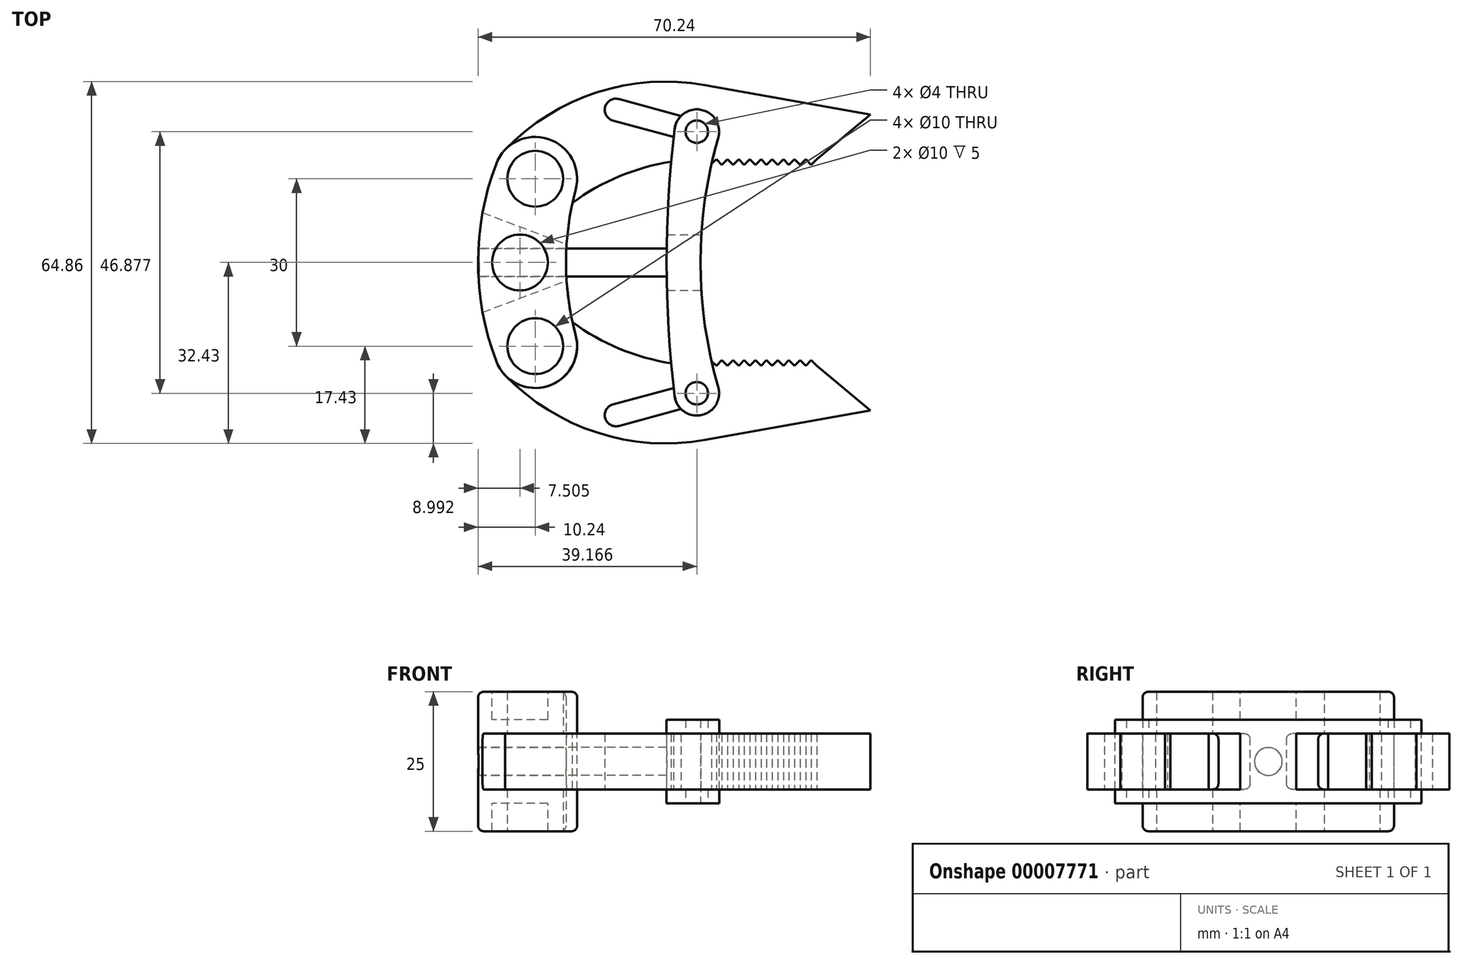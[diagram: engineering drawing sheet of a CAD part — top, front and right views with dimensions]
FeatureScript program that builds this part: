
annotation { "Feature Type Name" : "Feature", "Feature Type Description" : "" }
export const myFeature = defineFeature(function(context is Context, id is Id, definition is map)
    precondition{}
    {
        {
            var Q0;
            Q0=qCreatedBy(makeId("Top.planeOp"),FACE);
            var sketch = newSketch(context, id + "F0", { "sketchPlane" : qUnion([Q0])});
            skLineSegment(sketch, "E0", {"start": v(0, -15) * mm, "end": v(0, 15) * mm, "construction": true});
            skArc(sketch, "E1", {"start": v(7.24, 13.04) * mm, "mid": v(2.3, 22.14) * mm, "end": v(-7.02, 17.65) * mm});
            skArc(sketch, "E2", {"start": v(-7.02, -17.65) * mm, "mid": v(2.3, -22.14) * mm, "end": v(7.24, -13.04) * mm});
            skArc(sketch, "E3", {"start": v(-7.02, 17.65) * mm, "mid": v(-10.24, 0) * mm, "end": v(-7.02, -17.65) * mm});
            skArc(sketch, "E4", {"start": v(7.24, 13.04) * mm, "mid": v(5.5, 0) * mm, "end": v(7.24, -13.04) * mm});
            skCircle(sketch, "E5", {"center": v(0, 15) * mm, "radius": 5 * mm});
            skCircle(sketch, "E6", {"center": v(0, -15) * mm, "radius": 5 * mm});
            skSolve(sketch);
        }
        {
            var Q0;
            Q0=qCreatedBy(makeId("Top.planeOp"),FACE);
            var sketch = newSketch(context, id + "F1", { "sketchPlane" : qUnion([Q0])});
            skArc(sketch, "E7", {"start": v(-5.4, 20.2) * mm, "mid": v(-5.5, 9.9) * mm, "end": v(4.8, 9.24) * mm});
            skArc(sketch, "E8", {"start": v(30.42, 31.8) * mm, "mid": v(11.06, 30.48) * mm, "end": v(-5.4, 20.2) * mm});
            skLineSegment(sketch, "E9", {"start": v(30.42, 31.8) * mm, "end": v(60, 26.52) * mm});
            skArc(sketch, "E10", {"start": v(30.42, 18.52) * mm, "mid": v(16.8, 16.13) * mm, "end": v(4.8, 9.24) * mm});
            skLineSegment(sketch, "E11", {"start": v(30.42, 18.52) * mm, "end": v(50.42, 18.52) * mm, "construction": true});
            skLineSegment(sketch, "E12", {"start": v(60, 26.52) * mm, "end": v(50.42, 18.52) * mm});
            skCircle(sketch, "E13.0", {"center": v(0, 15) * mm, "radius": 5 * mm});
            skLineSegment(sketch, "E14", {"start": v(0, 0) * mm, "end": v(62.82, 0) * mm, "construction": true});
            skArc(sketch, "E15.0.MirrorCS", {"start": v(-5.4, -20.2) * mm, "mid": v(-5.5, -9.9) * mm, "end": v(4.8, -9.24) * mm});
            skArc(sketch, "E15.1.MirrorCS", {"start": v(30.42, -18.52) * mm, "mid": v(16.8, -16.13) * mm, "end": v(4.8, -9.24) * mm});
            skArc(sketch, "E15.2.MirrorCS", {"start": v(30.42, -31.8) * mm, "mid": v(11.06, -30.48) * mm, "end": v(-5.4, -20.2) * mm});
            skCircle(sketch, "E15.3.MirrorC", {"center": v(0, -15) * mm, "radius": 5 * mm});
            skLineSegment(sketch, "E15.4.MirrorCS", {"start": v(60, -26.52) * mm, "end": v(50.42, -18.52) * mm});
            skLineSegment(sketch, "E15.5.MirrorCS", {"start": v(30.42, -18.52) * mm, "end": v(50.42, -18.52) * mm, "construction": true});
            skLineSegment(sketch, "E15.6.MirrorCS", {"start": v(30.42, -31.8) * mm, "end": v(60, -26.52) * mm});
            skLineSegment(sketch, "E16", {"start": v(30.42, -18.52) * mm, "end": v(31.42, -17.52) * mm});
            skLineSegment(sketch, "E17", {"start": v(31.42, -17.52) * mm, "end": v(32.42, -18.52) * mm});
            skLineSegment(sketch, "E18.1.0.0", {"start": v(32.42, -18.52) * mm, "end": v(33.42, -17.52) * mm});
            skLineSegment(sketch, "E18.1.0.1", {"start": v(33.42, -17.52) * mm, "end": v(34.42, -18.52) * mm});
            skLineSegment(sketch, "E18.2.0.0", {"start": v(34.42, -18.52) * mm, "end": v(35.42, -17.52) * mm});
            skLineSegment(sketch, "E18.2.0.1", {"start": v(35.42, -17.52) * mm, "end": v(36.42, -18.52) * mm});
            skLineSegment(sketch, "E18.3.0.0", {"start": v(36.42, -18.52) * mm, "end": v(37.42, -17.52) * mm});
            skLineSegment(sketch, "E18.3.0.1", {"start": v(37.42, -17.52) * mm, "end": v(38.42, -18.52) * mm});
            skLineSegment(sketch, "E18.4.0.0", {"start": v(38.42, -18.52) * mm, "end": v(39.42, -17.52) * mm});
            skLineSegment(sketch, "E18.4.0.1", {"start": v(39.42, -17.52) * mm, "end": v(40.42, -18.52) * mm});
            skLineSegment(sketch, "E18.5.0.0", {"start": v(40.42, -18.52) * mm, "end": v(41.42, -17.52) * mm});
            skLineSegment(sketch, "E18.5.0.1", {"start": v(41.42, -17.52) * mm, "end": v(42.42, -18.52) * mm});
            skLineSegment(sketch, "E18.6.0.0", {"start": v(42.42, -18.52) * mm, "end": v(43.42, -17.52) * mm});
            skLineSegment(sketch, "E18.6.0.1", {"start": v(43.42, -17.52) * mm, "end": v(44.42, -18.52) * mm});
            skLineSegment(sketch, "E18.7.0.0", {"start": v(44.42, -18.52) * mm, "end": v(45.42, -17.52) * mm});
            skLineSegment(sketch, "E18.7.0.1", {"start": v(45.42, -17.52) * mm, "end": v(46.42, -18.52) * mm});
            skLineSegment(sketch, "E18.8.0.0", {"start": v(46.42, -18.52) * mm, "end": v(47.42, -17.52) * mm});
            skLineSegment(sketch, "E18.8.0.1", {"start": v(47.42, -17.52) * mm, "end": v(48.42, -18.52) * mm});
            skLineSegment(sketch, "E18.9.0.0", {"start": v(48.42, -18.52) * mm, "end": v(49.42, -17.52) * mm});
            skLineSegment(sketch, "E18.9.0.1", {"start": v(49.42, -17.52) * mm, "end": v(50.42, -18.52) * mm});
            skLineSegment(sketch, "E18.direction1", {"start": v(30.42, -18.52) * mm, "end": v(32.42, -18.52) * mm, "construction": true});
            skLineSegment(sketch, "E19", {"start": v(30.42, 18.52) * mm, "end": v(31.42, 17.52) * mm});
            skLineSegment(sketch, "E20", {"start": v(31.42, 17.52) * mm, "end": v(32.42, 18.52) * mm});
            skLineSegment(sketch, "E21.1.0.0", {"start": v(32.42, 18.52) * mm, "end": v(33.42, 17.52) * mm});
            skLineSegment(sketch, "E21.1.0.1", {"start": v(33.42, 17.52) * mm, "end": v(34.42, 18.52) * mm});
            skLineSegment(sketch, "E21.2.0.0", {"start": v(34.42, 18.52) * mm, "end": v(35.42, 17.52) * mm});
            skLineSegment(sketch, "E21.2.0.1", {"start": v(35.42, 17.52) * mm, "end": v(36.42, 18.52) * mm});
            skLineSegment(sketch, "E21.3.0.0", {"start": v(36.42, 18.52) * mm, "end": v(37.42, 17.52) * mm});
            skLineSegment(sketch, "E21.3.0.1", {"start": v(37.42, 17.52) * mm, "end": v(38.42, 18.52) * mm});
            skLineSegment(sketch, "E21.4.0.0", {"start": v(38.42, 18.52) * mm, "end": v(39.42, 17.52) * mm});
            skLineSegment(sketch, "E21.4.0.1", {"start": v(39.42, 17.52) * mm, "end": v(40.42, 18.52) * mm});
            skLineSegment(sketch, "E21.5.0.0", {"start": v(40.42, 18.52) * mm, "end": v(41.42, 17.52) * mm});
            skLineSegment(sketch, "E21.5.0.1", {"start": v(41.42, 17.52) * mm, "end": v(42.42, 18.52) * mm});
            skLineSegment(sketch, "E21.6.0.0", {"start": v(42.42, 18.52) * mm, "end": v(43.42, 17.52) * mm});
            skLineSegment(sketch, "E21.6.0.1", {"start": v(43.42, 17.52) * mm, "end": v(44.42, 18.52) * mm});
            skLineSegment(sketch, "E21.7.0.0", {"start": v(44.42, 18.52) * mm, "end": v(45.42, 17.52) * mm});
            skLineSegment(sketch, "E21.7.0.1", {"start": v(45.42, 17.52) * mm, "end": v(46.42, 18.52) * mm});
            skLineSegment(sketch, "E21.8.0.0", {"start": v(46.42, 18.52) * mm, "end": v(47.42, 17.52) * mm});
            skLineSegment(sketch, "E21.8.0.1", {"start": v(47.42, 17.52) * mm, "end": v(48.42, 18.52) * mm});
            skLineSegment(sketch, "E21.9.0.0", {"start": v(48.42, 18.52) * mm, "end": v(49.42, 17.52) * mm});
            skLineSegment(sketch, "E21.9.0.1", {"start": v(49.42, 17.52) * mm, "end": v(50.42, 18.52) * mm});
            skLineSegment(sketch, "E21.direction1", {"start": v(31.42, 17.52) * mm, "end": v(33.42, 17.52) * mm, "construction": true});
            skArc(sketch, "E22", {"start": v(14.97, 29.28) * mm, "mid": v(12.52, 27.88) * mm, "end": v(13.92, 25.42) * mm});
            skArc(sketch, "E23", {"start": v(28.4, 21.5) * mm, "mid": v(30.86, 22.92) * mm, "end": v(29.45, 25.37) * mm});
            skLineSegment(sketch, "E24", {"start": v(14.97, 29.28) * mm, "end": v(29.45, 25.37) * mm});
            skLineSegment(sketch, "E25", {"start": v(13.92, 25.42) * mm, "end": v(28.4, 21.5) * mm});
            skLineSegment(sketch, "E26", {"start": v(14.45, 27.35) * mm, "end": v(28.93, 23.44) * mm, "construction": true});
            skArc(sketch, "E27.1.MirrorCS", {"start": v(13.92, 25.42) * mm, "mid": v(12.52, 27.88) * mm, "end": v(14.97, 29.28) * mm});
            skArc(sketch, "E27.2.MirrorCS", {"start": v(29.45, 25.37) * mm, "mid": v(30.86, 22.92) * mm, "end": v(28.4, 21.5) * mm});
            skArc(sketch, "E28.0.MirrorCS", {"start": v(29.45, -25.37) * mm, "mid": v(30.86, -22.92) * mm, "end": v(28.4, -21.5) * mm});
            skLineSegment(sketch, "E28.1.MirrorCS", {"start": v(14.97, -29.28) * mm, "end": v(29.45, -25.37) * mm});
            skArc(sketch, "E28.2.MirrorCS", {"start": v(14.97, -29.28) * mm, "mid": v(12.52, -27.88) * mm, "end": v(13.92, -25.42) * mm});
            skLineSegment(sketch, "E28.3.MirrorCS", {"start": v(13.92, -25.42) * mm, "end": v(28.4, -21.5) * mm});
            skLineSegment(sketch, "E29", {"start": v(30.42, 31.8) * mm, "end": v(28.93, 23.44) * mm, "construction": true});
            skSolve(sketch);
        }
        {
            var Q0;
            Q0 = qSketchRegion(id + "F0", true);
            extrude(context, id + "F2", {"entities" : qUnion([Q0]), "endBound" : BoundingType.SYMMETRIC, "depth" : 25 * mm});
        }
        {
            var Q0;
            Q0 = qSketchRegion(id + "F1", true);
            extrude(context, id + "F3", {"entities" : qUnion([Q0]), "endBound" : BoundingType.SYMMETRIC, "depth" : 10 * mm});
        }
        {
            var Q0;
            Q0=makeQuery(id+"F2.opExtrude","CAP_FACE",FACE,{"disambiguationData":[OSD([sQuery(id+"F0.wireOp",EDGE,"E1"),sQuery(id+"F0.wireOp",EDGE,"E2"),sQuery(id+"F0.wireOp",EDGE,"E3"),sQuery(id+"F0.wireOp",EDGE,"E4"),sQuery(id+"F0.wireOp",EDGE,"E5"),sQuery(id+"F0.wireOp",EDGE,"E6")])],"isStart":false});
            var sketch = newSketch(context, id + "F4", { "sketchPlane" : qUnion([Q0])});
            skArc(sketch, "E30", {"start": v(0, 15) * mm, "mid": v(-2.74, 0) * mm, "end": v(0, -15) * mm, "construction": true});
            skCircle(sketch, "E31", {"center": v(-2.74, 0) * mm, "radius": 5 * mm});
            skSolve(sketch);
        }
        {
            var Q0;
            Q0 = qSketchRegion(id + "F4", true);
            extrude(context, id + "F5", {"entities" : qUnion([Q0]), "operationType" : NewBodyOperationType.REMOVE, "endBound" : BoundingType.THROUGH_ALL, "oppositeDirection" : true, "depth" : 25 * mm});
        }
        {
            var Q0;
            Q0=qCreatedBy(makeId("Top.planeOp"),FACE);
            var sketch = newSketch(context, id + "F6", { "sketchPlane" : qUnion([Q0])});
            skCircle(sketch, "E32.0", {"center": v(-2.74, 0) * mm, "radius": 6 * mm, "construction": true});
            skCircle(sketch, "E33", {"center": v(0, 15) * mm, "radius": 9 * mm, "construction": true});
            skLineSegment(sketch, "E34", {"start": v(-9.43, 8.94) * mm, "end": v(5.62, 3.26) * mm});
            skArc(sketch, "E35.0", {"start": v(-7.02, 17.65) * mm, "mid": v(-8.42, 13.35) * mm, "end": v(-9.43, 8.94) * mm});
            skArc(sketch, "E36.0", {"start": v(7.24, 13.04) * mm, "mid": v(6.18, 8.2) * mm, "end": v(5.62, 3.26) * mm});
            skPoint(sketch, "E37.orphan", {"position": v(-7.02, -17.65) * mm});
            skPoint(sketch, "E38.orphan", {"position": v(7.24, -13.04) * mm});
            skLineSegment(sketch, "E39", {"start": v(-2.74, 0) * mm, "end": v(16.54, 0) * mm, "construction": true});
            skLineSegment(sketch, "E40.0.MirrorCS", {"start": v(-9.43, -8.94) * mm, "end": v(5.62, -3.26) * mm});
            skArc(sketch, "E41.0", {"start": v(7.24, 13.04) * mm, "mid": v(2.3, 22.14) * mm, "end": v(-7.02, 17.65) * mm});
            skArc(sketch, "E42.0", {"start": v(-7.02, -17.65) * mm, "mid": v(2.3, -22.14) * mm, "end": v(7.24, -13.04) * mm});
            skArc(sketch, "E43.0.MirrorCS", {"start": v(7.24, -13.04) * mm, "mid": v(6.18, -8.2) * mm, "end": v(5.62, -3.26) * mm});
            skArc(sketch, "E43.1.MirrorCS", {"start": v(-7.02, -17.65) * mm, "mid": v(-8.42, -13.35) * mm, "end": v(-9.43, -8.94) * mm});
            skSolve(sketch);
        }
        {
            var Q0;
            Q0 = qSketchRegion(id + "F6", true);
            extrude(context, id + "F7", {"entities" : qUnion([Q0]), "operationType" : NewBodyOperationType.REMOVE, "endBound" : BoundingType.SYMMETRIC, "oppositeDirection" : true, "depth" : 10 * mm});
        }
        {
            var Q0;
            Q0=qCreatedBy(makeId("Top.planeOp"),FACE);
            var sketch = newSketch(context, id + "F8", { "sketchPlane" : qUnion([Q0])});
            skCircle(sketch, "E44.0", {"center": v(-2.74, 0) * mm, "radius": 5 * mm});
            skSolve(sketch);
        }
        {
            var Q0;
            Q0 = qSketchRegion(id + "F8", true);
            extrude(context, id + "F9", {"entities" : qUnion([Q0]), "operationType" : NewBodyOperationType.ADD, "endBound" : BoundingType.SYMMETRIC, "depth" : 15 * mm});
        }
        {
            var Q0;
            Q0=qCreatedBy(makeId("Right.planeOp"),FACE);
            var sketch = newSketch(context, id + "F10", { "sketchPlane" : qUnion([Q0])});
            skCircle(sketch, "E45", {"center": v(0, 0) * mm, "radius": 2.5 * mm});
            skSolve(sketch);
        }
        {
            var Q0;
            Q0 = qSketchRegion(id + "F10", true);
            extrude(context, id + "F11", {"entities" : qUnion([Q0]), "operationType" : NewBodyOperationType.REMOVE, "endBound" : BoundingType.THROUGH_ALL, "oppositeDirection" : true, "depth" : 25 * mm, "hasSecondDirection" : true, "secondDirectionBound" : SecondDirectionBoundingType.THROUGH_ALL, "secondDirectionOppositeDirection" : false, "secondDirectionDepth" : 25 * mm});
        }
        {
            var Q0;
            Q0=qCreatedBy(makeId("Right.planeOp"),FACE);
            var sketch = newSketch(context, id + "F12", { "sketchPlane" : qUnion([Q0])});
            skCircle(sketch, "E46.0", {"center": v(0, 0) * mm, "radius": 2.5 * mm});
            skSolve(sketch);
        }
        {
            var Q0;
            Q0 = qSketchRegion(id + "F12", true);
            extrude(context, id + "F13", {"entities" : qUnion([Q0]), "depth" : 27 * mm, "hasSecondDirection" : true, "secondDirectionOppositeDirection" : true, "secondDirectionDepth" : 10 * mm});
        }
        {
            var Q0;
            Q0=qCreatedBy(makeId("Top.planeOp"),FACE);
            var sketch = newSketch(context, id + "F14", { "sketchPlane" : qUnion([Q0])});
            skLineSegment(sketch, "E47", {"start": v(0, 0) * mm, "end": v(36.42, 0) * mm, "construction": true});
            skArc(sketch, "E48", {"start": v(32.77, 22.32) * mm, "mid": v(29.73, 27.36) * mm, "end": v(24.95, 23.92) * mm});
            skArc(sketch, "E49", {"start": v(24.95, 23.92) * mm, "mid": v(23.52, 0) * mm, "end": v(24.95, -23.92) * mm});
            skArc(sketch, "E50.0.MirrorC", {"start": v(32.77, -22.32) * mm, "mid": v(29.73, -27.36) * mm, "end": v(24.95, -23.92) * mm});
            skArc(sketch, "E51", {"start": v(32.77, 22.32) * mm, "mid": v(29.59, 0) * mm, "end": v(32.77, -22.32) * mm});
            skCircle(sketch, "E52", {"center": v(28.93, 23.44) * mm, "radius": 2 * mm});
            skCircle(sketch, "E53.0.MirrorC", {"center": v(28.93, -23.44) * mm, "radius": 2 * mm});
            skSolve(sketch);
        }
        {
            var Q0;
            Q0 = qSketchRegion(id + "F14", true);
            extrude(context, id + "F15", {"entities" : qUnion([Q0]), "operationType" : NewBodyOperationType.ADD, "endBound" : BoundingType.SYMMETRIC, "depth" : 15 * mm});
        }
        {
            var Q0;
            Q0=qCreatedBy(makeId("Top.planeOp"),FACE);
            var sketch = newSketch(context, id + "F16", { "sketchPlane" : qUnion([Q0])});
            skArc(sketch, "E54.0.0", {"start": v(32.77, -22.32) * mm, "mid": v(30.78, -13.74) * mm, "end": v(29.75, -5) * mm});
            skArc(sketch, "E54.0.1", {"start": v(32.77, 22.32) * mm, "mid": v(29.73, 27.36) * mm, "end": v(24.95, 23.92) * mm});
            skArc(sketch, "E54.0.2", {"start": v(24.95, 23.92) * mm, "mid": v(24.04, 14.47) * mm, "end": v(23.58, 5) * mm});
            skArc(sketch, "E54.0.3", {"start": v(24.95, -23.92) * mm, "mid": v(29.73, -27.36) * mm, "end": v(32.77, -22.32) * mm});
            skLineSegment(sketch, "E55", {"start": v(0, 0) * mm, "end": v(223.52, 0) * mm, "construction": true});
            skLineSegment(sketch, "E56", {"start": v(23.58, 5) * mm, "end": v(29.75, 5) * mm});
            skLineSegment(sketch, "E57.0.MirrorCS", {"start": v(23.58, -5) * mm, "end": v(29.75, -5) * mm});
            skArc(sketch, "E58.trimOffspring", {"start": v(29.75, 5) * mm, "mid": v(30.78, 13.74) * mm, "end": v(32.77, 22.32) * mm});
            skArc(sketch, "E59.trimOffspring", {"start": v(23.58, -5) * mm, "mid": v(24.04, -14.47) * mm, "end": v(24.95, -23.92) * mm});
            skSolve(sketch);
        }
        {
            var Q0;
            Q0 = qSketchRegion(id + "F16", true);
            extrude(context, id + "F17", {"entities" : qUnion([Q0]), "operationType" : NewBodyOperationType.REMOVE, "endBound" : BoundingType.SYMMETRIC, "oppositeDirection" : true, "depth" : 10 * mm});
        }
        {
            var Q0;
            Q0=makeQuery(id+"F7.boolean.opBoolean","COPY",EDGE,{"derivedFrom":makeQuery(id+"F7.opExtrude","CAP_EDGE",EDGE,{"disambiguationData":[OSD([sQuery(id+"F6.wireOp",EDGE,"E34")])],"isStart":true})});
            var Q1;
            Q1=makeQuery(id+"F7.boolean.opBoolean","COPY",EDGE,{"derivedFrom":makeQuery(id+"F7.opExtrude","CAP_EDGE",EDGE,{"disambiguationData":[OSD([sQuery(id+"F6.wireOp",EDGE,"E34")])],"isStart":false})});
            var Q2;
            Q2=makeQuery(id+"F7.boolean.opBoolean","COPY",EDGE,{"derivedFrom":makeQuery(id+"F7.opExtrude","CAP_EDGE",EDGE,{"disambiguationData":[OSD([sQuery(id+"F6.wireOp",EDGE,"E40.0.MirrorCS")])],"isStart":false})});
            var Q3;
            Q3=makeQuery(id+"F7.boolean.opBoolean","COPY",EDGE,{"derivedFrom":makeQuery(id+"F7.opExtrude","CAP_EDGE",EDGE,{"disambiguationData":[OSD([sQuery(id+"F6.wireOp",EDGE,"E40.0.MirrorCS")])],"isStart":true})});
            var Q4;
            Q4=makeQuery(id+"F7.boolean.opBoolean","COPY",EDGE,{"derivedFrom":makeQuery(id+"F7.opExtrude","SWEPT_EDGE",EDGE,{"disambiguationData":[OSD([sQuery(id+"F6.wireOp",EDGE,"E34"),sQuery(id+"F6.wireOp",EDGE,"E36.0")])]})});
            var Q5;
            Q5=makeQuery(id+"F7.boolean.opBoolean","COPY",EDGE,{"derivedFrom":makeQuery(id+"F7.opExtrude","SWEPT_EDGE",EDGE,{"disambiguationData":[OSD([sQuery(id+"F6.wireOp",EDGE,"E40.0.MirrorCS"),sQuery(id+"F6.wireOp",EDGE,"E43.0.MirrorCS")])]})});
            var Q6;
            Q6=makeQuery(id+"F2.opExtrude","CAP_EDGE",EDGE,{"disambiguationData":[OSD([sQuery(id+"F0.wireOp",EDGE,"E4")])],"isStart":true});
            var Q7;
            Q7=makeQuery(id+"F2.opExtrude","CAP_EDGE",EDGE,{"disambiguationData":[OSD([sQuery(id+"F0.wireOp",EDGE,"E4")])],"isStart":false});
            fillet(context, id + "F18", {"entities" : qUnion([Q0, Q1, Q2, Q3, Q4, Q5, Q6, Q7]), "radius" : 1 * mm, "tangentPropagation" : true, "allowEdgeOverflow" : false});
        }
    });
